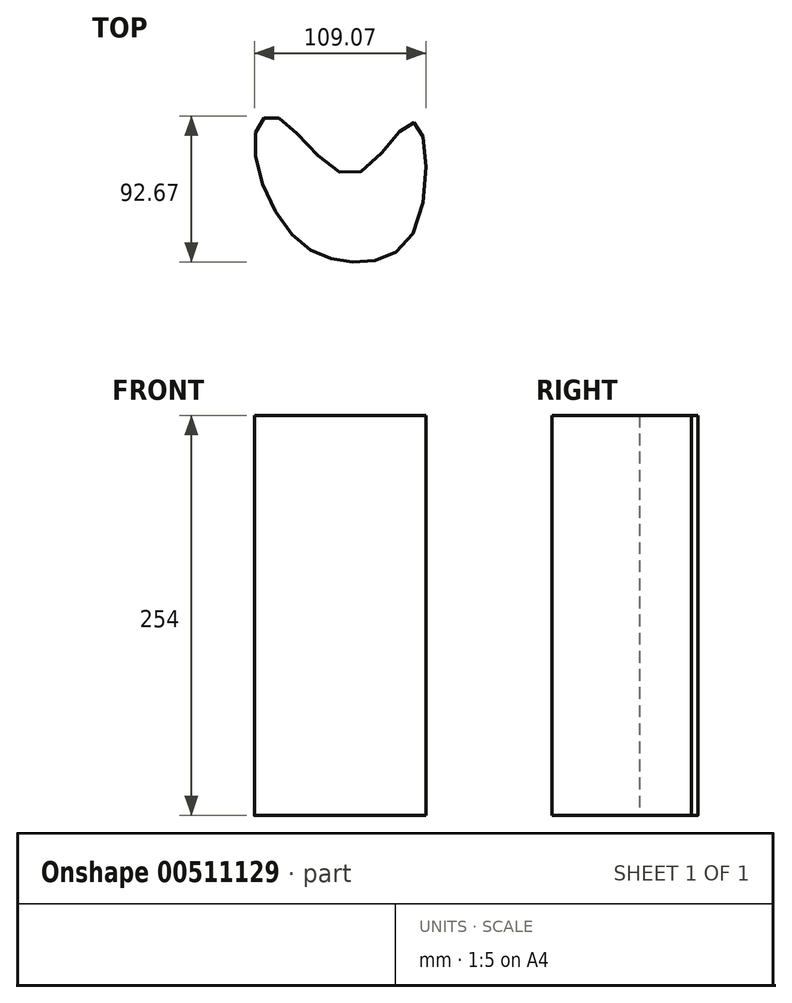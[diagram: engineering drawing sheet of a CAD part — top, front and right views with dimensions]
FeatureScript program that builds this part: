
annotation { "Feature Type Name" : "Feature", "Feature Type Description" : "" }
export const myFeature = defineFeature(function(context is Context, id is Id, definition is map)
    precondition{}
    {
        {
            var Q0;
            Q0=qCreatedBy(makeId("Top.planeOp"),FACE);
            var sketch = newSketch(context, id + "F0", { "sketchPlane" : qUnion([Q0])});
            skFitSpline(sketch, "E0", {"points": [v(-61.74, 38.75) * mm, v(-40.1, -24.25) * mm, v(0, -43.37) * mm, v(39.51, -23) * mm, v(38.57, 45.02) * mm, v(0, 12.11) * mm, v(-47.32, 48.16) * mm, v(-61.74, 38.75) * mm]});
            skSolve(sketch);
        }
        {
            var Q0;
            Q0=makeQuery(id+"F0.imprint","IMPRINT",FACE,{"disambiguationData":[TD([[makeQuery(id+"F0.imprint","IMPRINT",EDGE,{"derivedFrom":sQuery(id+"F0.wireOp",EDGE,"E0")}),1.0]])]});
            extrude(context, id + "F1", {"entities" : qUnion([Q0]), "depth" : 254 * mm});
        }
    });
